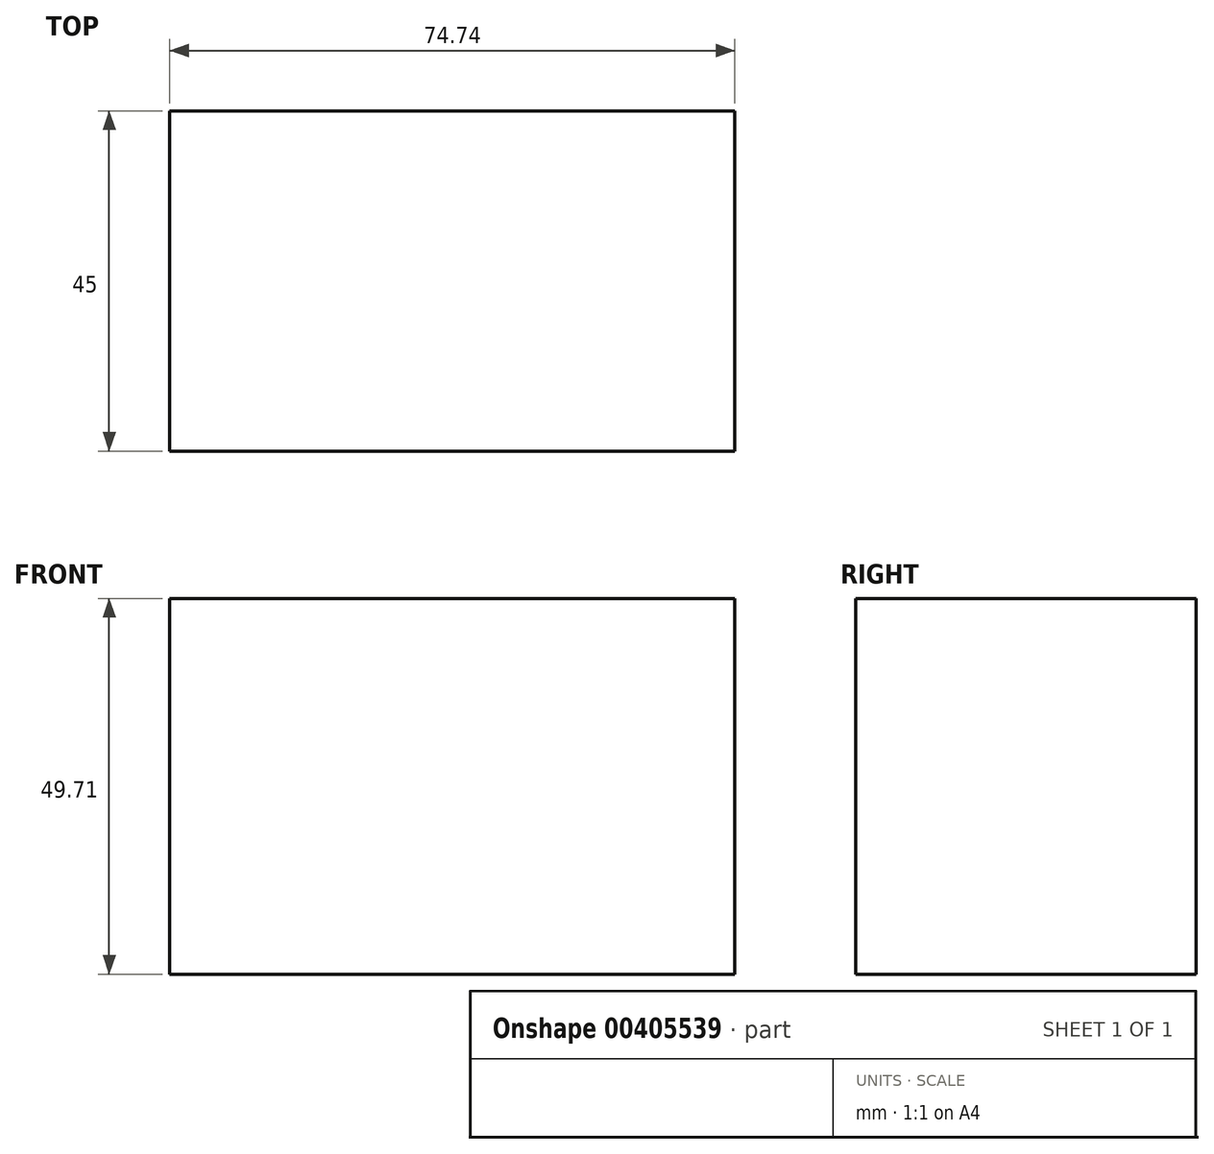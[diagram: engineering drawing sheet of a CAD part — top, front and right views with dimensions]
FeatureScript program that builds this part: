
annotation { "Feature Type Name" : "Feature", "Feature Type Description" : "" }
export const myFeature = defineFeature(function(context is Context, id is Id, definition is map)
    precondition{}
    {
        {
            var Q0;
            Q0=qCreatedBy(makeId("Front.planeOp"),FACE);
            var sketch = newSketch(context, id + "F0", { "sketchPlane" : qUnion([Q0])});
            skLineSegment(sketch, "E0.bottom", {"start": v(-5.35, 0) * mm, "end": v(69.39, 0) * mm});
            skLineSegment(sketch, "E0.top", {"start": v(-5.35, 49.7) * mm, "end": v(69.39, 49.7) * mm});
            skLineSegment(sketch, "E0.left", {"start": v(-5.35, 0) * mm, "end": v(-5.35, 49.7) * mm});
            skLineSegment(sketch, "E0.right", {"start": v(69.39, 0) * mm, "end": v(69.39, 49.7) * mm});
            skSolve(sketch);
        }
        {
            var Q0;
            Q0=makeQuery(id+"F0.imprint","IMPRINT",FACE,{"disambiguationData":[TD([[makeQuery(id+"F0.imprint","IMPRINT",EDGE,{"derivedFrom":sQuery(id+"F0.wireOp",EDGE,"E0.bottom")}),1.0]])]});
            extrude(context, id + "F1", {"entities" : qUnion([Q0]), "depth" : 45 * mm});
        }
    });
